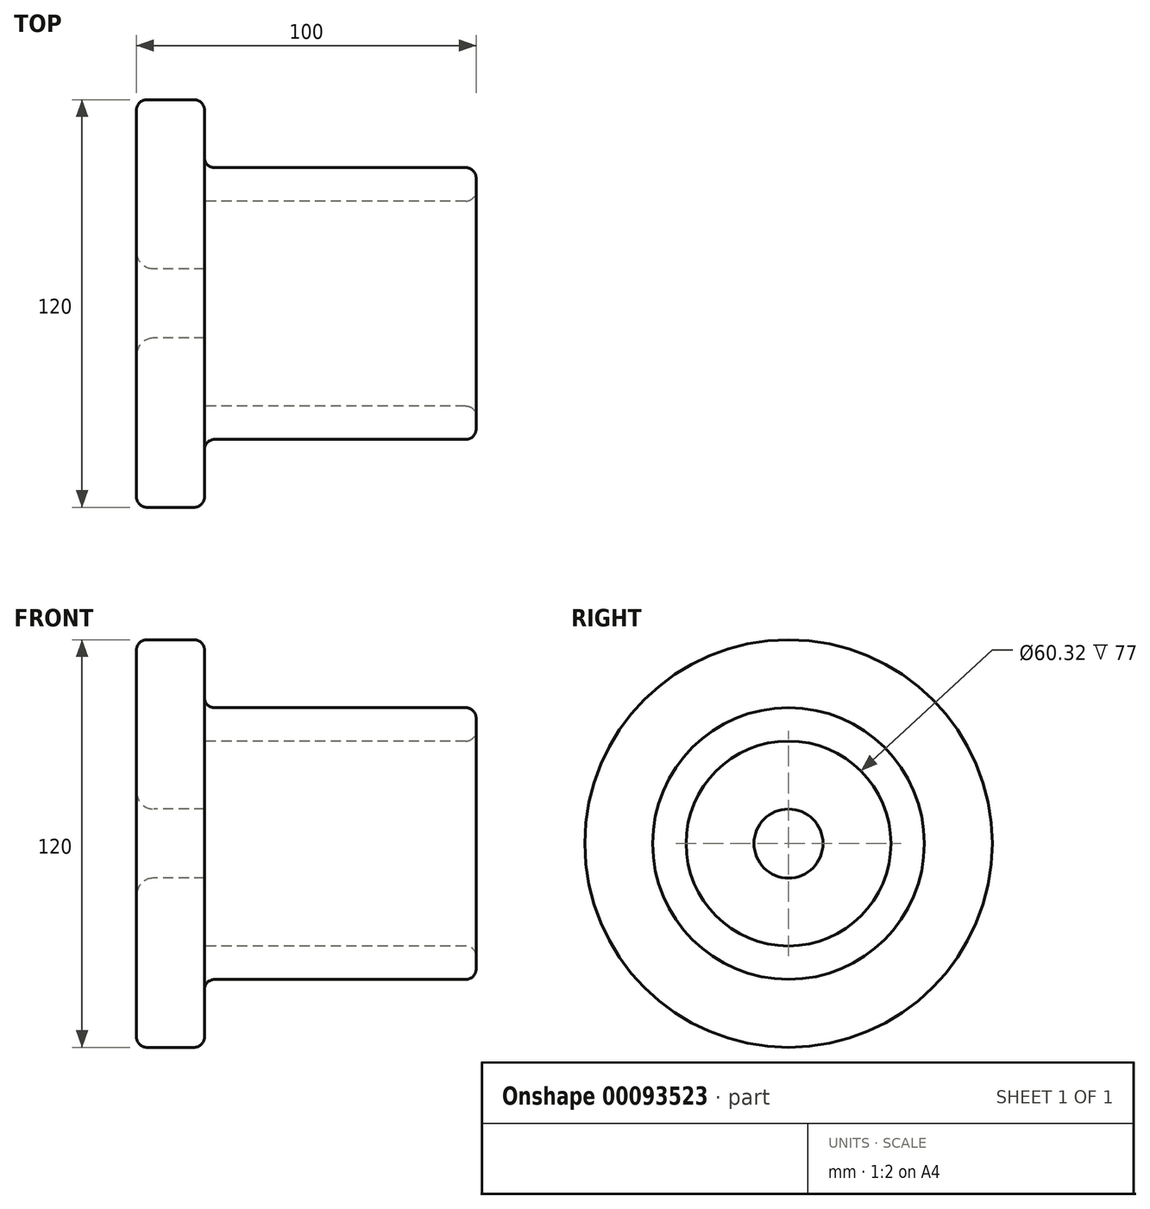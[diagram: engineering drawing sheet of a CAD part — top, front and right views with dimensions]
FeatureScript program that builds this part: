
annotation { "Feature Type Name" : "Feature", "Feature Type Description" : "" }
export const myFeature = defineFeature(function(context is Context, id is Id, definition is map)
    precondition{}
    {
        {
            var Q0;
            Q0=qCreatedBy(makeId("Front.planeOp"),FACE);
            var sketch = newSketch(context, id + "F0", { "sketchPlane" : qUnion([Q0])});
            skLineSegment(sketch, "E0", {"start": v(-16.74, 0) * mm, "end": v(18, 0) * mm, "construction": true});
            skLineSegment(sketch, "E1", {"start": v(-16.74, 0) * mm, "end": v(-16.74, 4.26) * mm});
            skLineSegment(sketch, "E2", {"start": v(-16.74, 4.26) * mm, "end": v(-10.83, 4.26) * mm});
            skLineSegment(sketch, "E3", {"start": v(-10.83, 4.26) * mm, "end": v(-10.83, 1.76) * mm});
            skLineSegment(sketch, "E4", {"start": v(-10.83, 1.76) * mm, "end": v(-4.92, 1.76) * mm});
            skLineSegment(sketch, "E5", {"start": v(-4.92, 1.76) * mm, "end": v(-4.92, 8.86) * mm});
            skLineSegment(sketch, "E6", {"start": v(-4.92, 8.86) * mm, "end": v(0, 8.86) * mm});
            skLineSegment(sketch, "E7", {"start": v(0, 8.86) * mm, "end": v(0, 10.44) * mm});
            skLineSegment(sketch, "E8", {"start": v(0, 10.44) * mm, "end": v(1, 10.44) * mm});
            skLineSegment(sketch, "E9", {"start": v(1, 10.44) * mm, "end": v(1, 7.96) * mm});
            skLineSegment(sketch, "E10", {"start": v(1, 7.96) * mm, "end": v(5.1, 7.96) * mm});
            skLineSegment(sketch, "E11", {"start": v(5.1, 7.96) * mm, "end": v(5.1, 5.9) * mm});
            skLineSegment(sketch, "E12", {"start": v(5.1, 5.9) * mm, "end": v(12.02, 5.9) * mm, "construction": true});
            skLineSegment(sketch, "E13", {"start": v(5.1, 5.9) * mm, "end": v(5.1, 5.4) * mm, "construction": true});
            skLineSegment(sketch, "E14", {"start": v(5.1, 5.4) * mm, "end": v(12.02, 5.4) * mm, "construction": true});
            skLineSegment(sketch, "E15", {"start": v(5.1, 5.4) * mm, "end": v(6.1, 5.4) * mm, "construction": true});
            skLineSegment(sketch, "E16", {"start": v(6.1, 5.4) * mm, "end": v(7.1, 5.4) * mm, "construction": true});
            skLineSegment(sketch, "E17", {"start": v(7.1, 5.9) * mm, "end": v(8.09, 5.9) * mm, "construction": true});
            skLineSegment(sketch, "E18", {"start": v(8.09, 5.9) * mm, "end": v(9.08, 5.9) * mm, "construction": true});
            skLineSegment(sketch, "E19", {"start": v(9.08, 5.9) * mm, "end": v(10.07, 5.9) * mm, "construction": true});
            skLineSegment(sketch, "E20", {"start": v(10.07, 5.9) * mm, "end": v(11.06, 5.9) * mm, "construction": true});
            skLineSegment(sketch, "E21", {"start": v(11.06, 5.9) * mm, "end": v(12.02, 5.9) * mm, "construction": true});
            skLineSegment(sketch, "E22.0", {"start": v(5.1, 5.92) * mm, "end": v(6.1, 5.92) * mm});
            skLineSegment(sketch, "E23.0", {"start": v(7.1, 5.4) * mm, "end": v(8.09, 5.4) * mm});
            skLineSegment(sketch, "E24.0", {"start": v(8.09, 5.4) * mm, "end": v(9.08, 5.4) * mm});
            skLineSegment(sketch, "E25.0", {"start": v(10.07, 5.4) * mm, "end": v(11.06, 5.4) * mm});
            skLineSegment(sketch, "E26", {"start": v(5.1, 5.9) * mm, "end": v(5.6, 5.92) * mm, "construction": true});
            skLineSegment(sketch, "E27", {"start": v(6.1, 5.92) * mm, "end": v(6.6, 5.9) * mm, "construction": true});
            skPoint(sketch, "E27.endSnap0", {"position": v(6.6, 5.4) * mm});
            skLineSegment(sketch, "E28", {"start": v(5.1, 5.4) * mm, "end": v(5.6, 5.4) * mm, "construction": true});
            skLineSegment(sketch, "E29", {"start": v(7.1, 5.9) * mm, "end": v(7.6, 5.9) * mm, "construction": true});
            skLineSegment(sketch, "E30", {"start": v(7.1, 5.4) * mm, "end": v(7.6, 5.4) * mm, "construction": true});
            skLineSegment(sketch, "E31", {"start": v(8.09, 5.9) * mm, "end": v(8.58, 5.9) * mm, "construction": true});
            skLineSegment(sketch, "E32", {"start": v(8.09, 5.4) * mm, "end": v(8.56, 5.41) * mm, "construction": true});
            skLineSegment(sketch, "E33", {"start": v(9.08, 5.4) * mm, "end": v(9.57, 5.4) * mm, "construction": true});
            skPoint(sketch, "E33.endSnap0", {"position": v(9.57, 5.9) * mm});
            skLineSegment(sketch, "E34", {"start": v(10.07, 5.4) * mm, "end": v(10.56, 5.4) * mm, "construction": true});
            skLineSegment(sketch, "E35", {"start": v(10.07, 5.9) * mm, "end": v(10.56, 5.9) * mm, "construction": true});
            skLineSegment(sketch, "E36", {"start": v(11.06, 5.9) * mm, "end": v(11.54, 5.9) * mm, "construction": true});
            skLineSegment(sketch, "E37", {"start": v(11.06, 5.4) * mm, "end": v(11.54, 5.41) * mm, "construction": true});
            skLineSegment(sketch, "E38", {"start": v(5.1, 5.4) * mm, "end": v(5.6, 5.92) * mm});
            skLineSegment(sketch, "E39", {"start": v(5.6, 5.92) * mm, "end": v(6.1, 5.4) * mm});
            skLineSegment(sketch, "E40", {"start": v(6.1, 5.4) * mm, "end": v(6.6, 5.9) * mm});
            skLineSegment(sketch, "E41", {"start": v(6.6, 5.9) * mm, "end": v(7.1, 5.4) * mm});
            skLineSegment(sketch, "E42", {"start": v(7.1, 5.4) * mm, "end": v(7.6, 5.9) * mm});
            skLineSegment(sketch, "E43", {"start": v(7.6, 5.91) * mm, "end": v(8.09, 5.4) * mm});
            skLineSegment(sketch, "E44", {"start": v(8.09, 5.4) * mm, "end": v(8.58, 5.91) * mm});
            skLineSegment(sketch, "E45", {"start": v(8.58, 5.9) * mm, "end": v(9.1, 5.4) * mm});
            skLineSegment(sketch, "E46", {"start": v(9.1, 5.4) * mm, "end": v(9.57, 5.9) * mm});
            skLineSegment(sketch, "E47", {"start": v(9.57, 5.91) * mm, "end": v(10.07, 5.4) * mm});
            skLineSegment(sketch, "E48", {"start": v(10.07, 5.4) * mm, "end": v(10.56, 5.9) * mm});
            skLineSegment(sketch, "E49", {"start": v(10.56, 5.9) * mm, "end": v(11.06, 5.4) * mm});
            skLineSegment(sketch, "E50", {"start": v(11.06, 5.4) * mm, "end": v(11.54, 5.9) * mm});
            skLineSegment(sketch, "E51", {"start": v(11.54, 5.9) * mm, "end": v(12.02, 5.41) * mm});
            skLineSegment(sketch, "E52", {"start": v(12.02, 5.4) * mm, "end": v(12.02, 5.16) * mm});
            skLineSegment(sketch, "E53", {"start": v(12.02, 5.16) * mm, "end": v(16.34, 5.16) * mm});
            skLineSegment(sketch, "E54", {"start": v(16.34, 5.16) * mm, "end": v(16.34, 5.06) * mm});
            skLineSegment(sketch, "E55", {"start": v(16.34, 5.06) * mm, "end": v(22.95, 5.06) * mm});
            skLineSegment(sketch, "E56", {"start": v(18, 0) * mm, "end": v(22.95, 0) * mm, "construction": true});
            skLineSegment(sketch, "E57", {"start": v(22.95, 5.06) * mm, "end": v(22.95, 0) * mm});
            skLineSegment(sketch, "E58", {"start": v(5.1, 5.4) * mm, "end": v(5.1, 5.9) * mm});
            skSolve(sketch);
        }
        {
            var Q0;
            Q0=sQuery(id+"F0.wireOp",EDGE,"E1");
            var Q1;
            Q1=sQuery(id+"F0.wireOp",EDGE,"E2");
            var Q2;
            Q2=sQuery(id+"F0.wireOp",EDGE,"E3");
            var Q3;
            Q3=sQuery(id+"F0.wireOp",EDGE,"E4");
            var Q4;
            Q4=sQuery(id+"F0.wireOp",EDGE,"E5");
            var Q5;
            Q5=sQuery(id+"F0.wireOp",EDGE,"E6");
            var Q6;
            Q6=sQuery(id+"F0.wireOp",EDGE,"E7");
            var Q7;
            Q7=sQuery(id+"F0.wireOp",EDGE,"E8");
            var Q8;
            Q8=sQuery(id+"F0.wireOp",EDGE,"E9");
            var Q9;
            Q9=sQuery(id+"F0.wireOp",EDGE,"E10");
            var Q10;
            Q10=sQuery(id+"F0.wireOp",EDGE,"E11");
            var Q11;
            Q11=sQuery(id+"F0.wireOp",EDGE,"E38");
            var Q12;
            Q12=sQuery(id+"F0.wireOp",EDGE,"E39");
            var Q13;
            Q13=sQuery(id+"F0.wireOp",EDGE,"E40");
            var Q14;
            Q14=sQuery(id+"F0.wireOp",EDGE,"E41");
            var Q15;
            Q15=sQuery(id+"F0.wireOp",EDGE,"E42");
            var Q16;
            Q16=sQuery(id+"F0.wireOp",EDGE,"E43");
            var Q17;
            Q17=sQuery(id+"F0.wireOp",EDGE,"E44");
            var Q18;
            Q18=sQuery(id+"F0.wireOp",EDGE,"E45");
            var Q19;
            Q19=sQuery(id+"F0.wireOp",EDGE,"E46");
            var Q20;
            Q20=sQuery(id+"F0.wireOp",EDGE,"E47");
            var Q21;
            Q21=sQuery(id+"F0.wireOp",EDGE,"E48");
            var Q22;
            Q22=sQuery(id+"F0.wireOp",EDGE,"E49");
            var Q23;
            Q23=sQuery(id+"F0.wireOp",EDGE,"E50");
            var Q24;
            Q24=sQuery(id+"F0.wireOp",EDGE,"E51");
            var Q25;
            Q25=sQuery(id+"F0.wireOp",EDGE,"E52");
            var Q26;
            Q26=sQuery(id+"F0.wireOp",EDGE,"E53");
            var Q27;
            Q27=sQuery(id+"F0.wireOp",EDGE,"E54");
            var Q28;
            Q28=sQuery(id+"F0.wireOp",EDGE,"E55");
            var Q29;
            Q29=sQuery(id+"F0.wireOp",EDGE,"E57");
            var Q30;
            Q30=sQuery(id+"F0.wireOp",EDGE,"E56");
            revolve(context, id + "F1", {"bodyType" : ToolBodyType.SURFACE, "surfaceEntities" : qUnion([Q0, Q1, Q2, Q3, Q4, Q5, Q6, Q7, Q8, Q9, Q10, Q11, Q12, Q13, Q14, Q15, Q16, Q17, Q18, Q19, Q20, Q21, Q22, Q23, Q24, Q25, Q26, Q27, Q28, Q29]), "axis" : qUnion([Q30]), "revolveType" : RevolveType.FULL});
        }
        {
            var Q0;
            Q0=makeQuery(id+"F1.opRevolve","SWEPT_EDGE",EDGE,{"disambiguationData":[OSD([sQuery(id+"F0.wireOp",VERTEX,"E2.start")])]});
            var Q1;
            Q1=makeQuery(id+"F1.opRevolve","SWEPT_EDGE",EDGE,{"disambiguationData":[OSD([sQuery(id+"F0.wireOp",VERTEX,"E3.start")])]});
            var Q2;
            Q2=makeQuery(id+"F1.opRevolve","SWEPT_EDGE",EDGE,{"disambiguationData":[OSD([sQuery(id+"F0.wireOp",VERTEX,"E6.start")])]});
            var Q3;
            Q3=makeQuery(id+"F1.opRevolve","SWEPT_EDGE",EDGE,{"disambiguationData":[OSD([sQuery(id+"F0.wireOp",VERTEX,"E57.start")])]});
            fillet(context, id + "F2", {"entities" : qUnion([Q0, Q1, Q2, Q3]), "radius" : 1 * mm, "tangentPropagation" : true, "allowEdgeOverflow" : false});
        }
        {
            var Q0;
            Q0=qCreatedBy(makeId("Front.planeOp"),FACE);
            var sketch = newSketch(context, id + "F3", { "sketchPlane" : qUnion([Q0])});
            skLineSegment(sketch, "E59", {"start": v(-47.33, -137.5) * mm, "end": v(52.67, -137.5) * mm, "construction": true});
            skLineSegment(sketch, "E60", {"start": v(-47.33, -137.5) * mm, "end": v(-47.33, -77.5) * mm});
            skLineSegment(sketch, "E61", {"start": v(-47.33, -77.5) * mm, "end": v(-27.33, -77.5) * mm});
            skLineSegment(sketch, "E62", {"start": v(-27.33, -77.5) * mm, "end": v(-27.33, -97.5) * mm});
            skLineSegment(sketch, "E63", {"start": v(-27.33, -97.5) * mm, "end": v(52.67, -97.5) * mm});
            skLineSegment(sketch, "E64", {"start": v(52.67, -97.5) * mm, "end": v(52.67, -137.5) * mm});
            skLineSegment(sketch, "E65", {"start": v(52.67, -107.34) * mm, "end": v(-27.33, -107.34) * mm});
            skLineSegment(sketch, "E66", {"start": v(-27.33, -107.34) * mm, "end": v(-27.33, -127.34) * mm});
            skLineSegment(sketch, "E67", {"start": v(-27.33, -127.34) * mm, "end": v(-47.33, -127.34) * mm});
            skSolve(sketch);
        }
        {
            var Q0;
            Q0 = qSketchRegion(id + "F3", true);
            var Q1;
            Q1=sQuery(id+"F3.wireOp",EDGE,"E59");
            revolve(context, id + "F4", {"entities" : qUnion([Q0]), "axis" : qUnion([Q1]), "revolveType" : RevolveType.FULL});
        }
        {
            var Q0;
            Q0=makeQuery(id+"F4.opRevolve","SWEPT_EDGE",EDGE,{"disambiguationData":[OSD([sQuery(id+"F3.wireOp",EDGE,"E64"),sQuery(id+"F3.wireOp",EDGE,"E65")])]});
            var Q1;
            Q1=makeQuery(id+"F4.opRevolve","SWEPT_EDGE",EDGE,{"disambiguationData":[OSD([sQuery(id+"F3.wireOp",EDGE,"E63"),sQuery(id+"F3.wireOp",EDGE,"E64")])]});
            var Q2;
            Q2=makeQuery(id+"F4.opRevolve","SWEPT_EDGE",EDGE,{"disambiguationData":[OSD([sQuery(id+"F3.wireOp",EDGE,"E62"),sQuery(id+"F3.wireOp",EDGE,"E63")])]});
            var Q3;
            Q3=makeQuery(id+"F4.opRevolve","SWEPT_EDGE",EDGE,{"disambiguationData":[OSD([sQuery(id+"F3.wireOp",EDGE,"E61"),sQuery(id+"F3.wireOp",EDGE,"E62")])]});
            var Q4;
            Q4=makeQuery(id+"F4.opRevolve","SWEPT_EDGE",EDGE,{"disambiguationData":[OSD([sQuery(id+"F3.wireOp",EDGE,"E60"),sQuery(id+"F3.wireOp",EDGE,"E61")])]});
            fillet(context, id + "F5", {"entities" : qUnion([Q0, Q1, Q2, Q3, Q4]), "radius" : 3 * mm, "tangentPropagation" : true, "allowEdgeOverflow" : false});
        }
        {
            var Q0;
            Q0=makeQuery(id+"F4.opRevolve","SWEPT_EDGE",EDGE,{"disambiguationData":[OSD([sQuery(id+"F3.wireOp",EDGE,"E60"),sQuery(id+"F3.wireOp",EDGE,"E67")])]});
            fillet(context, id + "F6", {"entities" : qUnion([Q0]), "radius" : 5.08 * mm, "tangentPropagation" : true, "allowEdgeOverflow" : false});
        }
        {
            var Q0;
            Q0=makeQuery(id+"F1.opRevolve","SWEPT_EDGE",EDGE,{"disambiguationData":[OSD([sQuery(id+"F0.wireOp",VERTEX,"E9.start")])]});
            var Q1;
            Q1=makeQuery(id+"F1.opRevolve","SWEPT_EDGE",EDGE,{"disambiguationData":[OSD([sQuery(id+"F0.wireOp",VERTEX,"E8.start")])]});
            fillet(context, id + "F7", {"entities" : qUnion([Q0, Q1]), "radius" : .5 * mm, "tangentPropagation" : true, "allowEdgeOverflow" : false});
        }
    });
